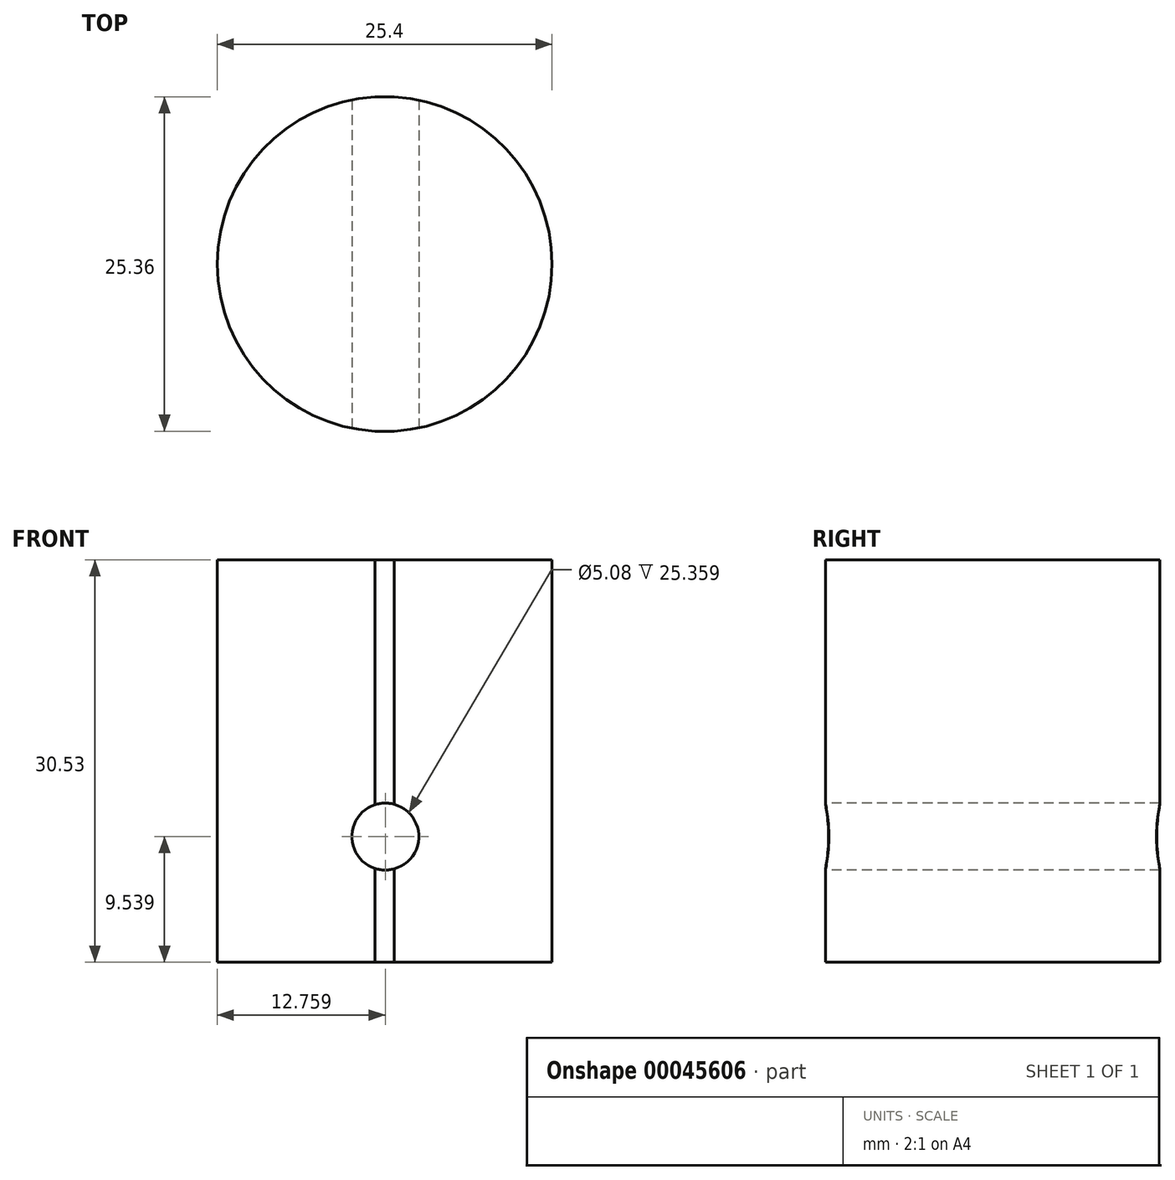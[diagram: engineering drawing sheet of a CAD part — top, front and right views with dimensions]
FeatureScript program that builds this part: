
annotation { "Feature Type Name" : "Feature", "Feature Type Description" : "" }
export const myFeature = defineFeature(function(context is Context, id is Id, definition is map)
    precondition{}
    {
        {
            var Q0;
            Q0=qCreatedBy(makeId("Top.planeOp"),FACE);
            var sketch = newSketch(context, id + "F0", { "sketchPlane" : qUnion([Q0])});
            skCircle(sketch, "E0", {"center": v(-46.05, 11.9) * mm, "radius": 12.7 * mm});
            skLineSegment(sketch, "E1.rect.bottom", {"start": v(-33.32, 24.57) * mm, "end": v(-58.78, 24.57) * mm});
            skLineSegment(sketch, "E1.rect.top", {"start": v(-33.32, -0.79) * mm, "end": v(-58.78, -0.79) * mm});
            skLineSegment(sketch, "E1.rect.left", {"start": v(-33.32, 24.57) * mm, "end": v(-33.32, -0.79) * mm});
            skLineSegment(sketch, "E1.rect.right", {"start": v(-58.78, 24.57) * mm, "end": v(-58.78, -0.79) * mm});
            skSolve(sketch);
        }
        {
            var Q0;
            Q0=makeQuery(id+"F0.imprint","IMPRINT",FACE,{"disambiguationData":[TD([[makeQuery(id+"F0.imprint","IMPRINT",EDGE,{"derivedFrom":sQuery(id+"F0.wireOp",EDGE,"E0")}),1.0]])]});
            extrude(context, id + "F1", {"entities" : qUnion([Q0]), "depth" : 30.53 * mm});
        }
        {
            var Q0;
            Q0=qCreatedBy(makeId("Front.planeOp"),FACE);
            var sketch = newSketch(context, id + "F2", { "sketchPlane" : qUnion([Q0])});
            skCircle(sketch, "E2", {"center": v(-46, 9.54) * mm, "radius": 2.54 * mm});
            skSolve(sketch);
        }
        {
            var Q0;
            Q0=makeQuery(id+"F2.imprint","IMPRINT",FACE,{"disambiguationData":[TD([[makeQuery(id+"F2.imprint","IMPRINT",EDGE,{"derivedFrom":sQuery(id+"F2.wireOp",EDGE,"E2")}),1.0]])]});
            extrude(context, id + "F3", {"entities" : qUnion([Q0]), "operationType" : NewBodyOperationType.REMOVE, "endBound" : BoundingType.SYMMETRIC, "oppositeDirection" : true, "depth" : 60.45 * mm});
        }
    });
